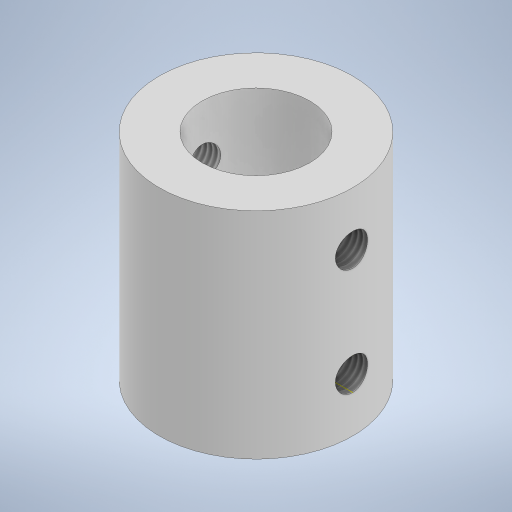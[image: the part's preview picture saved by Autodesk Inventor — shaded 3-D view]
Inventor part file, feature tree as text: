
AUTODESK INVENTOR PART (.ipt)
format: ipt  version: 2023 (Build 270158000, 158)  size: 256,512 bytes
history: native  units: mm
features: sketch x4, extrude x3, thread x2, other x1
ambient origin geometry x8: Origin, YZ Plane, XZ Plane, XY Plane, X Axis, Y Axis, Z Axis, Center Point
bodies: Body1 (feature_tree)
feature tree (10):
  other  "Твердое тело1"
  extrude  "Выдавливание1"  Depth=7.0mm
  extrude  "Выдавливание2"  Depth=18.0mm
  extrude  "Выдавливание3"  Depth=20.0mm TaperAngle=0.0deg
  thread  "Резьба1"
  thread  "Резьба2"
  sketch  "Эскиз4"
  sketch  "Эскиз1"
  sketch  "Эскиз2"
  sketch  "Эскиз3"
